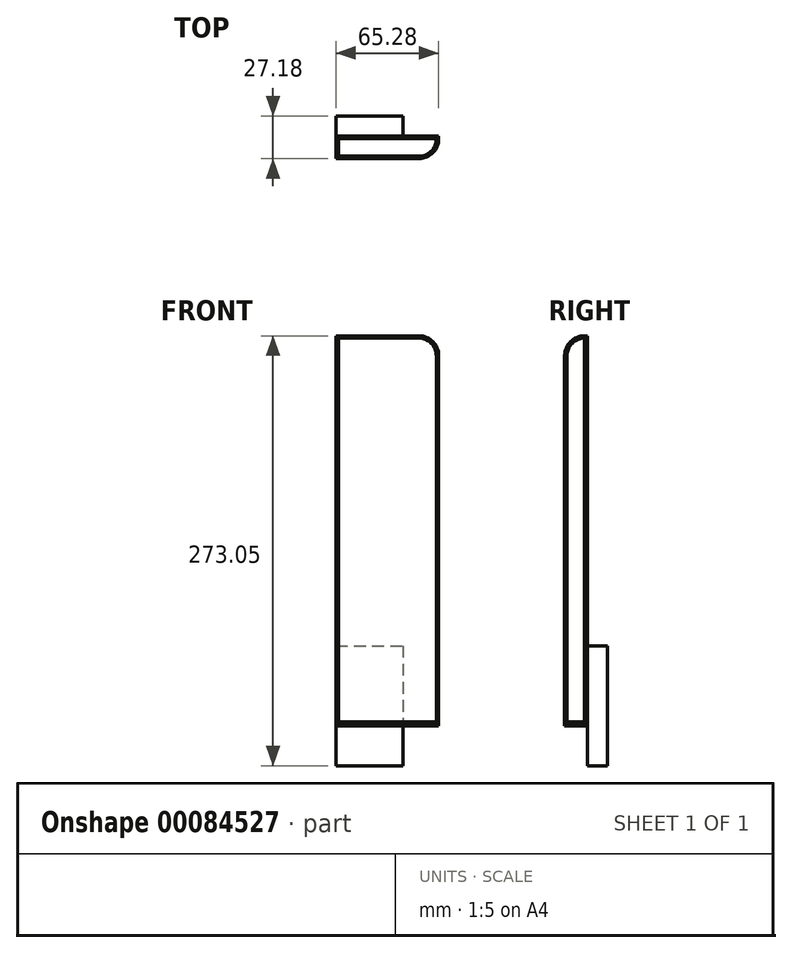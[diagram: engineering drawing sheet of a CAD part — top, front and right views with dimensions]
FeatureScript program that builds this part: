
annotation { "Feature Type Name" : "Feature", "Feature Type Description" : "" }
export const myFeature = defineFeature(function(context is Context, id is Id, definition is map)
    precondition{}
    {
        {
            var Q0;
            Q0=qCreatedBy(makeId("Front.planeOp"),FACE);
            var sketch = newSketch(context, id + "F0", { "sketchPlane" : qUnion([Q0])});
            skLineSegment(sketch, "E0.bottom", {"start": v(63.5, 247.65) * mm, "end": v(0, 247.65) * mm});
            skLineSegment(sketch, "E0.top", {"start": v(63.5, 0) * mm, "end": v(0, 0) * mm});
            skLineSegment(sketch, "E0.left", {"start": v(63.5, 247.65) * mm, "end": v(63.5, 0) * mm});
            skLineSegment(sketch, "E0.right", {"start": v(0, 247.65) * mm, "end": v(0, 0) * mm});
            skSolve(sketch);
        }
        {
            var Q0;
            Q0=qSketchRegion(id+"F0",true);
            extrude(context, id + "F1", {"entities" : qUnion([Q0]), "depth" : 1.78 * mm});
        }
        {
            var Q0;
            Q0=makeQuery(id+"F1.opExtrude","CAP_FACE",FACE,{"disambiguationData":[OSD([sQuery(id+"F0.wireOp",EDGE,"E0.bottom"),sQuery(id+"F0.wireOp",EDGE,"E0.top"),sQuery(id+"F0.wireOp",EDGE,"E0.left"),sQuery(id+"F0.wireOp",EDGE,"E0.right")])],"isStart":false});
            var sketch = newSketch(context, id + "F2", { "sketchPlane" : qUnion([Q0])});
            skLineSegment(sketch, "E1.bottom", {"start": v(0, 0) * mm, "end": v(63.5, 0) * mm});
            skLineSegment(sketch, "E1.top", {"start": v(0, 2.54) * mm, "end": v(63.5, 2.54) * mm});
            skLineSegment(sketch, "E1.left", {"start": v(0, 0) * mm, "end": v(0, 2.54) * mm});
            skLineSegment(sketch, "E1.right", {"start": v(63.5, 0) * mm, "end": v(63.5, 2.54) * mm});
            skSolve(sketch);
        }
        {
            var Q0;
            Q0=qSketchRegion(id+"F2",true);
            extrude(context, id + "F3", {"entities" : qUnion([Q0]), "operationType" : NewBodyOperationType.ADD, "depth" : 12.7 * mm});
        }
        {
            var Q0;
            Q0=makeQuery(id+"F3.boolean.opBoolean","MERGE",FACE,{"derivedFrom":[makeQuery(id+"F1.opExtrude","SWEPT_FACE",FACE,{"disambiguationData":[OSD([sQuery(id+"F0.wireOp",EDGE,"E0.left")])]}),makeQuery(id+"F3.opExtrude","SWEPT_FACE",FACE,{"disambiguationData":[OSD([sQuery(id+"F2.wireOp",EDGE,"E1.right")])]})]});
            var sketch = newSketch(context, id + "F4", { "sketchPlane" : qUnion([Q0])});
            skLineSegment(sketch, "E2.bottom", {"start": v(0, 0) * mm, "end": v(-14.48, 0) * mm});
            skLineSegment(sketch, "E2.top", {"start": v(0, 247.65) * mm, "end": v(-14.48, 247.65) * mm});
            skLineSegment(sketch, "E2.left", {"start": v(0, 0) * mm, "end": v(0, 247.65) * mm});
            skLineSegment(sketch, "E2.right", {"start": v(-14.48, 0) * mm, "end": v(-14.48, 247.65) * mm});
            skSolve(sketch);
        }
        {
            var Q0;
            Q0=qSketchRegion(id+"F4",true);
            extrude(context, id + "F5", {"entities" : qUnion([Q0]), "operationType" : NewBodyOperationType.ADD, "depth" : 1.78 * mm});
        }
        {
            var Q0;
            Q0=makeQuery(id+"F5.boolean.opBoolean","MERGE",FACE,{"derivedFrom":[makeQuery(id+"F1.opExtrude","CAP_FACE",FACE,{"disambiguationData":[OSD([sQuery(id+"F0.wireOp",EDGE,"E0.bottom"),sQuery(id+"F0.wireOp",EDGE,"E0.top"),sQuery(id+"F0.wireOp",EDGE,"E0.left"),sQuery(id+"F0.wireOp",EDGE,"E0.right")])],"isStart":true}),makeQuery(id+"F5.opExtrude","SWEPT_FACE",FACE,{"disambiguationData":[OSD([sQuery(id+"F4.wireOp",EDGE,"E2.left")])]})]});
            var sketch = newSketch(context, id + "F6", { "sketchPlane" : qUnion([Q0])});
            skLineSegment(sketch, "E3.bottom", {"start": v(-65.28, 50.8) * mm, "end": v(-22.6, 50.8) * mm});
            skLineSegment(sketch, "E3.top", {"start": v(-65.28, -25.4) * mm, "end": v(-22.6, -25.4) * mm});
            skLineSegment(sketch, "E3.left", {"start": v(-65.28, 50.8) * mm, "end": v(-65.28, -25.4) * mm});
            skLineSegment(sketch, "E3.right", {"start": v(-22.6, 50.8) * mm, "end": v(-22.6, -25.4) * mm});
            skSolve(sketch);
        }
        {
            var Q0;
            Q0=qSketchRegion(id+"F6",true);
            extrude(context, id + "F7", {"entities" : qUnion([Q0]), "operationType" : NewBodyOperationType.ADD, "depth" : 12.7 * mm});
        }
        {
            var Q0;
            Q0=makeQuery(id+"F1.opExtrude","SWEPT_EDGE",EDGE,{"disambiguationData":[OSD([sQuery(id+"F0.wireOp",EDGE,"E0.bottom"),sQuery(id+"F0.wireOp",EDGE,"E0.right")])]});
            var Q1;
            Q1=makeQuery(id+"F5.opExtrude","SWEPT_EDGE",EDGE,{"disambiguationData":[OSD([sQuery(id+"F4.wireOp",EDGE,"E2.top"),sQuery(id+"F4.wireOp",EDGE,"E2.right")])]});
            fillet(context, id + "F8", {"entities" : qUnion([Q0, Q1]), "radius" : 12.7 * mm, "tangentPropagation" : true, "allowEdgeOverflow" : false});
        }
        {
            var Q0;
            Q0=makeQuery(id+"F3.opExtrude","CAP_EDGE",EDGE,{"disambiguationData":[OSD([sQuery(id+"F2.wireOp",EDGE,"E1.left")])],"isStart":false});
            fillet(context, id + "F9", {"entities" : qUnion([Q0]), "radius" : 12.7 * mm, "tangentPropagation" : true, "allowEdgeOverflow" : false});
        }
        {
            var Q0;
            Q0=makeQuery(id+"F1.opExtrude","CAP_EDGE",EDGE,{"disambiguationData":[OSD([sQuery(id+"F0.wireOp",EDGE,"E0.right")])],"isStart":false});
            var Q1;
            Q1=makeQuery(id+"F9.opFillet","BLEND_EDGE",EDGE,{"blendedFrom":[makeQuery(id+"F3.opExtrude","CAP_EDGE",EDGE,{"disambiguationData":[OSD([sQuery(id+"F2.wireOp",EDGE,"E1.left")])],"isStart":false}),makeQuery(id+"F3.opExtrude","SWEPT_FACE",FACE,{"disambiguationData":[OSD([sQuery(id+"F2.wireOp",EDGE,"E1.top")])]})],"blendedInto":[makeQuery(id+"F3.opExtrude","SWEPT_FACE",FACE,{"disambiguationData":[OSD([sQuery(id+"F2.wireOp",EDGE,"E1.top")])]})]});
            var Q2;
            Q2=makeQuery(id+"F5.opExtrude","CAP_EDGE",EDGE,{"disambiguationData":[OSD([sQuery(id+"F4.wireOp",EDGE,"E2.right")])],"isStart":true});
            chamfer(context, id + "F10", {"entities" : qUnion([Q0, Q1, Q2]), "width" : 1.52 * mm, "tangentPropagation" : true});
        }
        {
            var Q0;
            Q0=makeQuery(id+"F1.opExtrude","SWEPT_BODY",BODY,{"disambiguationData":[OSD([sQuery(id+"F0.wireOp",EDGE,"E0.bottom"),sQuery(id+"F0.wireOp",EDGE,"E0.top"),sQuery(id+"F0.wireOp",EDGE,"E0.left"),sQuery(id+"F0.wireOp",EDGE,"E0.right")])]});
            var Q1;
            Q1=makeQuery(id+"F7.boolean.opBoolean","MERGE",FACE,{"derivedFrom":[makeQuery(id+"F5.opExtrude","CAP_FACE",FACE,{"disambiguationData":[OSD([sQuery(id+"F4.wireOp",EDGE,"E2.bottom"),sQuery(id+"F4.wireOp",EDGE,"E2.top"),sQuery(id+"F4.wireOp",EDGE,"E2.left"),sQuery(id+"F4.wireOp",EDGE,"E2.right")])],"isStart":false}),makeQuery(id+"F7.opExtrude","SWEPT_FACE",FACE,{"disambiguationData":[OSD([sQuery(id+"F6.wireOp",EDGE,"E3.left")])]})]});
            mirror(context, id + "F11", {"entities" : qUnion([Q0]), "mirrorPlane" : qUnion([Q1])});
        }
        {
            var Q0;
            Q0=makeQuery(id+"F1.opExtrude","SWEPT_BODY",BODY,{"disambiguationData":[OSD([sQuery(id+"F0.wireOp",EDGE,"E0.bottom"),sQuery(id+"F0.wireOp",EDGE,"E0.top"),sQuery(id+"F0.wireOp",EDGE,"E0.left"),sQuery(id+"F0.wireOp",EDGE,"E0.right")])]});
            deleteBodies(context, id + "F12", {"entities" : qUnion([Q0])});
        }
    });
